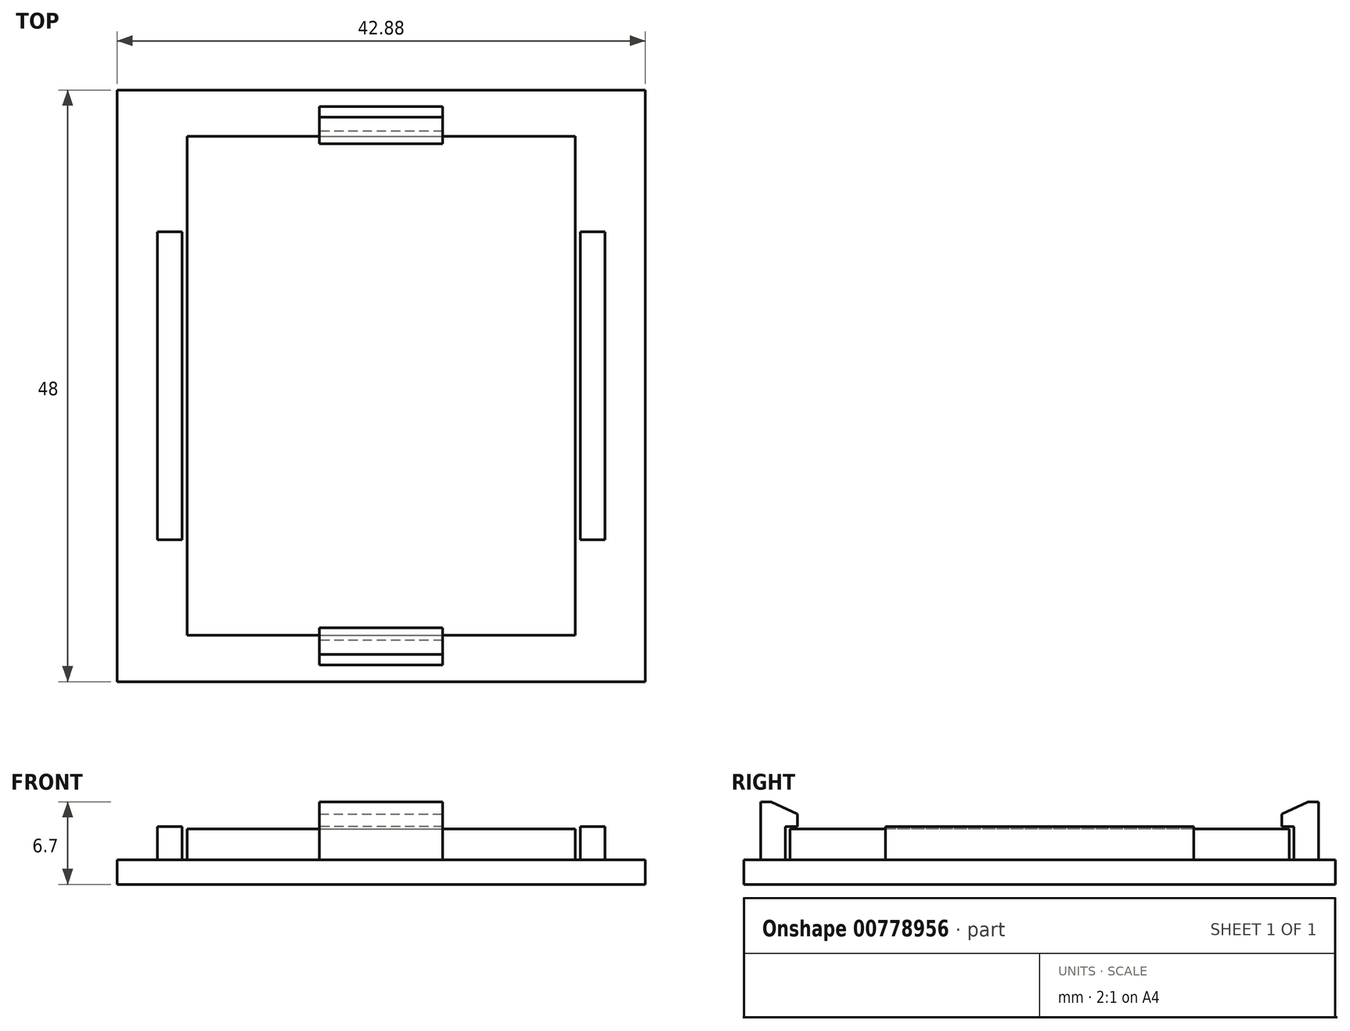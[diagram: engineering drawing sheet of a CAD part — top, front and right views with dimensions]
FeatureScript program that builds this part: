
annotation { "Feature Type Name" : "Feature", "Feature Type Description" : "" }
export const myFeature = defineFeature(function(context is Context, id is Id, definition is map)
    precondition{}
    {
        {
            var Q0;
            Q0=qCreatedBy(makeId("Top.planeOp"),FACE);
            var sketch = newSketch(context, id + "F0", { "sketchPlane" : qUnion([Q0])});
            skLineSegment(sketch, "E0.bottom", {"start": v(-15.75, 20.25) * mm, "end": v(15.75, 20.25) * mm});
            skLineSegment(sketch, "E0.top", {"start": v(-15.75, -20.25) * mm, "end": v(15.75, -20.25) * mm});
            skLineSegment(sketch, "E0.left", {"start": v(-15.75, 20.25) * mm, "end": v(-15.75, -20.25) * mm});
            skLineSegment(sketch, "E0.right", {"start": v(15.75, 20.25) * mm, "end": v(15.75, -20.25) * mm});
            skSolve(sketch);
        }
        {
            var Q0;
            Q0=makeQuery(id+"F0.imprint","IMPRINT",FACE,{"disambiguationData":[TD([[makeQuery(id+"F0.imprint","IMPRINT",EDGE,{"derivedFrom":sQuery(id+"F0.wireOp",EDGE,"E0.bottom")}),-1.0]])]});
            extrude(context, id + "F1", {"entities" : qUnion([Q0]), "depth" : 2.5 * mm, "offsetDistance" : 25 * mm});
        }
        {
            var Q0;
            Q0=qCreatedBy(makeId("Top.planeOp"),FACE);
            var sketch = newSketch(context, id + "F2", { "sketchPlane" : qUnion([Q0])});
            skLineSegment(sketch, "E1.bottom", {"start": v(16.15, 12.5) * mm, "end": v(18.15, 12.5) * mm});
            skLineSegment(sketch, "E1.top", {"start": v(16.15, -12.5) * mm, "end": v(18.15, -12.5) * mm});
            skLineSegment(sketch, "E1.left", {"start": v(16.15, 12.5) * mm, "end": v(16.15, -12.5) * mm});
            skLineSegment(sketch, "E1.right", {"start": v(18.15, 12.5) * mm, "end": v(18.15, -12.5) * mm});
            skLineSegment(sketch, "E2.bottom", {"start": v(5, -20.65) * mm, "end": v(-5, -20.65) * mm});
            skLineSegment(sketch, "E2.top", {"start": v(5, -22.65) * mm, "end": v(-5, -22.65) * mm});
            skLineSegment(sketch, "E2.left", {"start": v(5, -20.65) * mm, "end": v(5, -22.65) * mm});
            skLineSegment(sketch, "E2.right", {"start": v(-5, -20.65) * mm, "end": v(-5, -22.65) * mm});
            skLineSegment(sketch, "E3.MirrorCS", {"start": v(-16.15, -12.5) * mm, "end": v(-18.15, -12.5) * mm});
            skLineSegment(sketch, "E4.MirrorCS", {"start": v(-16.15, 12.5) * mm, "end": v(-18.15, 12.5) * mm});
            skLineSegment(sketch, "E5.MirrorCS", {"start": v(-16.15, 12.5) * mm, "end": v(-16.15, -12.5) * mm});
            skLineSegment(sketch, "E6.MirrorCS", {"start": v(-18.15, 12.5) * mm, "end": v(-18.15, -12.5) * mm});
            skLineSegment(sketch, "E7.MirrorCS", {"start": v(5, 20.65) * mm, "end": v(5, 22.65) * mm});
            skLineSegment(sketch, "E8.MirrorCS", {"start": v(5, 22.65) * mm, "end": v(-5, 22.65) * mm});
            skLineSegment(sketch, "E9.MirrorCS", {"start": v(-5, 20.65) * mm, "end": v(-5, 22.65) * mm});
            skLineSegment(sketch, "E10.MirrorCS", {"start": v(5, 20.65) * mm, "end": v(-5, 20.65) * mm});
            skSolve(sketch);
        }
        {
            var Q0;
            Q0 = qSketchRegion(id + "F2", true);
            extrude(context, id + "F3", {"entities" : qUnion([Q0]), "depth" : 2.7 * mm, "offsetDistance" : 25 * mm});
        }
        {
            var Q0;
            Q0=qCreatedBy(makeId("Top.planeOp"),FACE);
            var sketch = newSketch(context, id + "F4", { "sketchPlane" : qUnion([Q0])});
            skLineSegment(sketch, "E11.bottom", {"start": v(-21.44, 24) * mm, "end": v(21.44, 24) * mm});
            skLineSegment(sketch, "E11.top", {"start": v(-21.44, -24) * mm, "end": v(21.44, -24) * mm});
            skLineSegment(sketch, "E11.left", {"start": v(-21.44, 24) * mm, "end": v(-21.44, -24) * mm});
            skLineSegment(sketch, "E11.right", {"start": v(21.44, 24) * mm, "end": v(21.44, -24) * mm});
            skSolve(sketch);
        }
        {
            var Q0;
            Q0 = qSketchRegion(id + "F4", true);
            extrude(context, id + "F5", {"entities" : qUnion([Q0]), "operationType" : NewBodyOperationType.ADD, "oppositeDirection" : true, "depth" : 2 * mm, "offsetDistance" : 25 * mm});
        }
        {
            var Q0;
            Q0=makeQuery(id+"F3.opExtrude","CAP_FACE",FACE,{"disambiguationData":[OSD([sQuery(id+"F2.wireOp",EDGE,"E2.bottom"),sQuery(id+"F2.wireOp",EDGE,"E2.top"),sQuery(id+"F2.wireOp",EDGE,"E2.left"),sQuery(id+"F2.wireOp",EDGE,"E2.right")])],"isStart":false});
            var sketch = newSketch(context, id + "F6", { "sketchPlane" : qUnion([Q0])});
            skLineSegment(sketch, "E12.bottom", {"start": v(-5, -22.65) * mm, "end": v(5, -22.65) * mm});
            skLineSegment(sketch, "E12.top", {"start": v(-5, -19.65) * mm, "end": v(5, -19.65) * mm});
            skLineSegment(sketch, "E12.left", {"start": v(-5, -22.65) * mm, "end": v(-5, -19.65) * mm});
            skLineSegment(sketch, "E12.right", {"start": v(5, -22.65) * mm, "end": v(5, -19.65) * mm});
            skLineSegment(sketch, "E13.MirrorCS", {"start": v(-5, 22.65) * mm, "end": v(5, 22.65) * mm});
            skLineSegment(sketch, "E14.MirrorCS", {"start": v(-5, 19.65) * mm, "end": v(5, 19.65) * mm});
            skLineSegment(sketch, "E15.MirrorCS", {"start": v(5, 22.65) * mm, "end": v(5, 19.65) * mm});
            skLineSegment(sketch, "E16.MirrorCS", {"start": v(-5, 22.65) * mm, "end": v(-5, 19.65) * mm});
            skSolve(sketch);
        }
        {
            var Q0;
            Q0 = qSketchRegion(id + "F6", true);
            extrude(context, id + "F7", {"entities" : qUnion([Q0]), "operationType" : NewBodyOperationType.ADD, "depth" : 2 * mm, "offsetDistance" : 25 * mm});
        }
        {
            var Q0;
            Q0=makeQuery(id+"F7.opExtrude","CAP_EDGE",EDGE,{"disambiguationData":[OSD([sQuery(id+"F6.wireOp",EDGE,"E14.MirrorCS")])],"isStart":false});
            chamfer(context, id + "F8", {"entities" : qUnion([Q0]), "chamferType" : ChamferType.OFFSET_ANGLE, "width" : 1 * mm, "oppositeDirection" : true, "angle" : 65 * degree, "tangentPropagation" : true});
        }
        {
            var Q0;
            Q0=makeQuery(id+"F7.opExtrude","CAP_EDGE",EDGE,{"disambiguationData":[OSD([sQuery(id+"F6.wireOp",EDGE,"E12.top")])],"isStart":false});
            chamfer(context, id + "F9", {"entities" : qUnion([Q0]), "chamferType" : ChamferType.OFFSET_ANGLE, "width" : 1 * mm, "oppositeDirection" : false, "angle" : 65 * degree, "tangentPropagation" : true});
        }
    });
